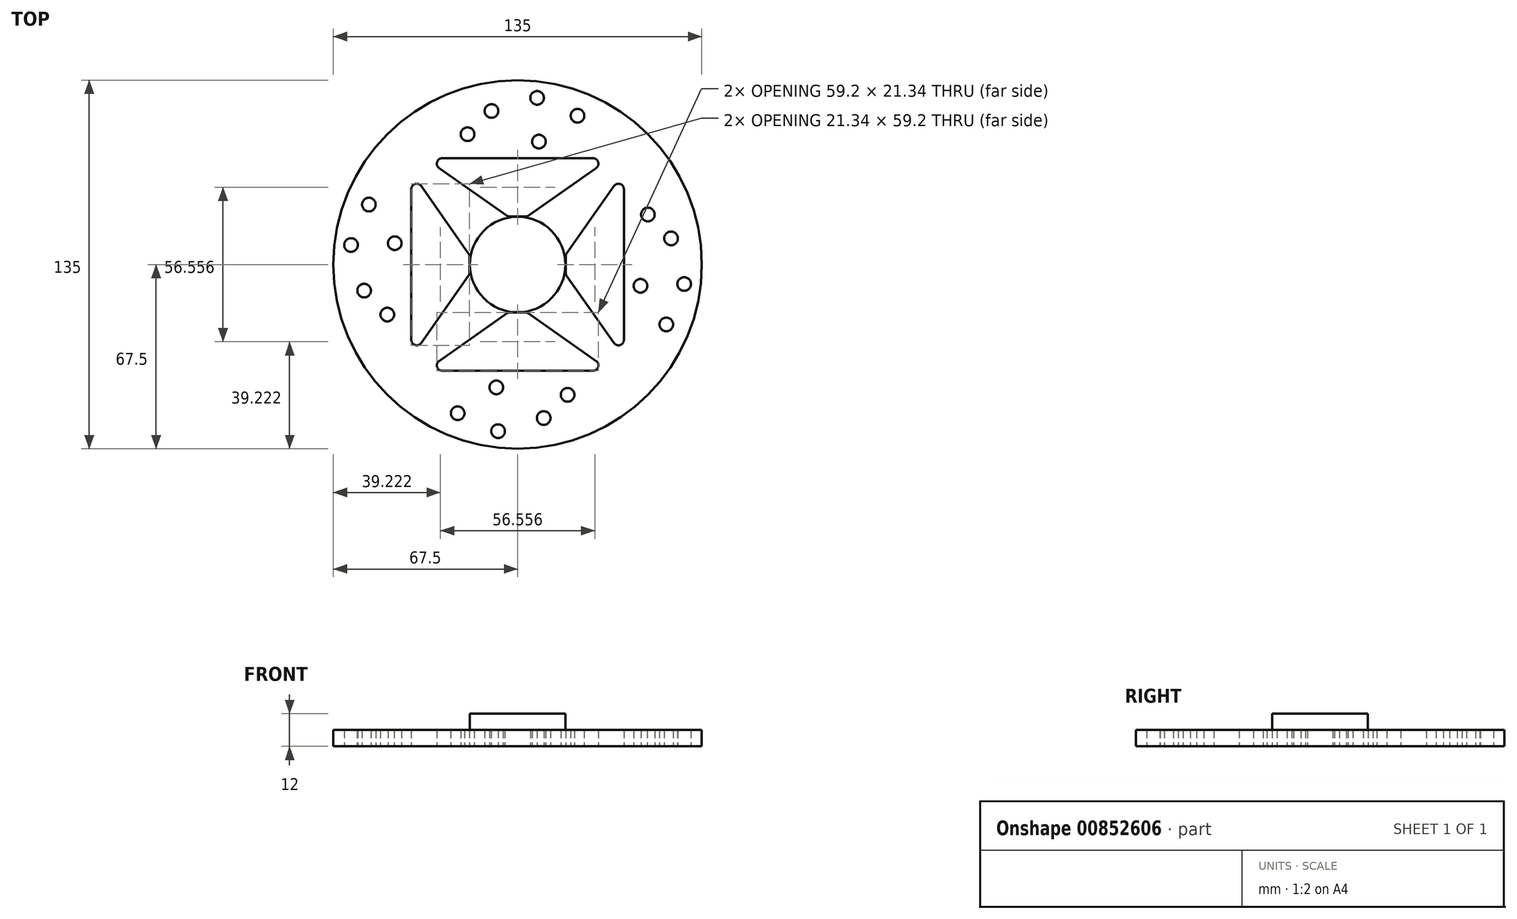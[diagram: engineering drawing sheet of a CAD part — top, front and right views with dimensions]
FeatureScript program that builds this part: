
annotation { "Feature Type Name" : "Feature", "Feature Type Description" : "" }
export const myFeature = defineFeature(function(context is Context, id is Id, definition is map)
    precondition{}
    {
        {
            var Q0;
            Q0=qCreatedBy(makeId("Top.planeOp"),FACE);
            var sketch = newSketch(context, id + "F0", { "sketchPlane" : qUnion([Q0])});
            skCircle(sketch, "E0", {"center": v(0, 0) * mm, "radius": 17.5 * mm});
            skCircle(sketch, "E1", {"center": v(0, 0) * mm, "radius": 67.5 * mm});
            skCircle(sketch, "E2", {"center": v(-18.33, 47.74) * mm, "radius": 2.5 * mm});
            skCircle(sketch, "E3", {"center": v(-9.56, 56.23) * mm, "radius": 2.5 * mm});
            skCircle(sketch, "E4", {"center": v(21.95, 54.5) * mm, "radius": 2.5 * mm});
            skCircle(sketch, "E5", {"center": v(7.15, 61.05) * mm, "radius": 2.5 * mm});
            skCircle(sketch, "E6", {"center": v(7.8, 45.02) * mm, "radius": 2.5 * mm});
            skLineSegment(sketch, "E7", {"start": v(4.08, 17.97) * mm, "end": v(28.75, 35.31) * mm});
            skLineSegment(sketch, "E8", {"start": v(27.6, 38.95) * mm, "end": v(0, 38.95) * mm});
            skLineSegment(sketch, "E9", {"start": v(2.93, 17.6) * mm, "end": v(0, 17.6) * mm});
            skPoint(sketch, "E10.visualSharp", {"position": v(3.56, 17.6) * mm});
            skArc(sketch, "E10.filletArc", {"start": v(2.93, 17.6) * mm, "mid": v(3.53, 17.7) * mm, "end": v(4.08, 17.97) * mm});
            skPoint(sketch, "E11.visualSharp", {"position": v(33.93, 38.95) * mm});
            skArc(sketch, "E11.filletArc", {"start": v(28.75, 35.31) * mm, "mid": v(29.5, 37.55) * mm, "end": v(27.6, 38.95) * mm});
            skLineSegment(sketch, "E12.MirrorCS", {"start": v(-27.6, 38.95) * mm, "end": v(0, 38.95) * mm});
            skArc(sketch, "E13.MirrorCS", {"start": v(-28.75, 35.31) * mm, "mid": v(-29.5, 37.55) * mm, "end": v(-27.6, 38.95) * mm});
            skLineSegment(sketch, "E14.MirrorCS", {"start": v(-4.08, 17.97) * mm, "end": v(-28.75, 35.31) * mm});
            skLineSegment(sketch, "E15.MirrorCS", {"start": v(-2.93, 17.6) * mm, "end": v(0, 17.6) * mm});
            skArc(sketch, "E16.MirrorCS", {"start": v(-2.93, 17.6) * mm, "mid": v(-3.53, 17.7) * mm, "end": v(-4.08, 17.97) * mm});
            skLineSegment(sketch, "E17.1.0", {"start": v(-17.6, 2.93) * mm, "end": v(-17.6, 0) * mm});
            skCircle(sketch, "E17.1.1", {"center": v(-45.02, 7.8) * mm, "radius": 2.5 * mm});
            skCircle(sketch, "E17.1.2", {"center": v(-61.05, 7.15) * mm, "radius": 2.5 * mm});
            skLineSegment(sketch, "E17.1.3", {"start": v(-38.95, 27.6) * mm, "end": v(-38.95, 0) * mm});
            skCircle(sketch, "E17.1.4", {"center": v(-47.74, -18.33) * mm, "radius": 2.5 * mm});
            skArc(sketch, "E17.1.5", {"start": v(-35.31, 28.75) * mm, "mid": v(-37.55, 29.5) * mm, "end": v(-38.95, 27.6) * mm});
            skLineSegment(sketch, "E17.1.6", {"start": v(-38.95, -27.6) * mm, "end": v(-38.95, 0) * mm});
            skLineSegment(sketch, "E17.1.7", {"start": v(-17.6, -2.93) * mm, "end": v(-17.6, 0) * mm});
            skCircle(sketch, "E17.1.8", {"center": v(-54.5, 21.95) * mm, "radius": 2.5 * mm});
            skLineSegment(sketch, "E17.1.9", {"start": v(-17.97, 4.08) * mm, "end": v(-35.31, 28.75) * mm});
            skCircle(sketch, "E17.1.10", {"center": v(-56.23, -9.56) * mm, "radius": 2.5 * mm});
            skLineSegment(sketch, "E17.1.11", {"start": v(-17.97, -4.08) * mm, "end": v(-35.31, -28.75) * mm});
            skArc(sketch, "E17.1.12", {"start": v(-35.31, -28.75) * mm, "mid": v(-37.55, -29.5) * mm, "end": v(-38.95, -27.6) * mm});
            skArc(sketch, "E17.1.13", {"start": v(-17.6, 2.93) * mm, "mid": v(-17.7, 3.53) * mm, "end": v(-17.97, 4.08) * mm});
            skArc(sketch, "E17.1.14", {"start": v(-17.6, -2.93) * mm, "mid": v(-17.7, -3.53) * mm, "end": v(-17.97, -4.08) * mm});
            skLineSegment(sketch, "E17.2.0", {"start": v(-2.93, -17.6) * mm, "end": v(0, -17.6) * mm});
            skCircle(sketch, "E17.2.1", {"center": v(-7.8, -45.02) * mm, "radius": 2.5 * mm});
            skCircle(sketch, "E17.2.2", {"center": v(-7.15, -61.05) * mm, "radius": 2.5 * mm});
            skLineSegment(sketch, "E17.2.3", {"start": v(-27.6, -38.95) * mm, "end": v(0, -38.95) * mm});
            skCircle(sketch, "E17.2.4", {"center": v(18.33, -47.74) * mm, "radius": 2.5 * mm});
            skArc(sketch, "E17.2.5", {"start": v(-28.75, -35.31) * mm, "mid": v(-29.5, -37.55) * mm, "end": v(-27.6, -38.95) * mm});
            skLineSegment(sketch, "E17.2.6", {"start": v(27.6, -38.95) * mm, "end": v(0, -38.95) * mm});
            skLineSegment(sketch, "E17.2.7", {"start": v(2.93, -17.6) * mm, "end": v(0, -17.6) * mm});
            skCircle(sketch, "E17.2.8", {"center": v(-21.95, -54.5) * mm, "radius": 2.5 * mm});
            skLineSegment(sketch, "E17.2.9", {"start": v(-4.08, -17.97) * mm, "end": v(-28.75, -35.31) * mm});
            skCircle(sketch, "E17.2.10", {"center": v(9.56, -56.23) * mm, "radius": 2.5 * mm});
            skLineSegment(sketch, "E17.2.11", {"start": v(4.08, -17.97) * mm, "end": v(28.75, -35.31) * mm});
            skArc(sketch, "E17.2.12", {"start": v(28.75, -35.31) * mm, "mid": v(29.5, -37.55) * mm, "end": v(27.6, -38.95) * mm});
            skArc(sketch, "E17.2.13", {"start": v(-2.93, -17.6) * mm, "mid": v(-3.53, -17.7) * mm, "end": v(-4.08, -17.97) * mm});
            skArc(sketch, "E17.2.14", {"start": v(2.93, -17.6) * mm, "mid": v(3.53, -17.7) * mm, "end": v(4.08, -17.97) * mm});
            skLineSegment(sketch, "E17.3.0", {"start": v(17.6, -2.93) * mm, "end": v(17.6, 0) * mm});
            skCircle(sketch, "E17.3.1", {"center": v(45.02, -7.8) * mm, "radius": 2.5 * mm});
            skCircle(sketch, "E17.3.2", {"center": v(61.05, -7.15) * mm, "radius": 2.5 * mm});
            skLineSegment(sketch, "E17.3.3", {"start": v(38.95, -27.6) * mm, "end": v(38.95, 0) * mm});
            skCircle(sketch, "E17.3.4", {"center": v(47.74, 18.33) * mm, "radius": 2.5 * mm});
            skArc(sketch, "E17.3.5", {"start": v(35.31, -28.75) * mm, "mid": v(37.55, -29.5) * mm, "end": v(38.95, -27.6) * mm});
            skLineSegment(sketch, "E17.3.6", {"start": v(38.95, 27.6) * mm, "end": v(38.95, 0) * mm});
            skLineSegment(sketch, "E17.3.7", {"start": v(17.6, 2.93) * mm, "end": v(17.6, 0) * mm});
            skCircle(sketch, "E17.3.8", {"center": v(54.5, -21.95) * mm, "radius": 2.5 * mm});
            skLineSegment(sketch, "E17.3.9", {"start": v(17.97, -4.08) * mm, "end": v(35.31, -28.75) * mm});
            skCircle(sketch, "E17.3.10", {"center": v(56.23, 9.56) * mm, "radius": 2.5 * mm});
            skLineSegment(sketch, "E17.3.11", {"start": v(17.97, 4.08) * mm, "end": v(35.31, 28.75) * mm});
            skArc(sketch, "E17.3.12", {"start": v(35.31, 28.75) * mm, "mid": v(37.55, 29.5) * mm, "end": v(38.95, 27.6) * mm});
            skArc(sketch, "E17.3.13", {"start": v(17.6, -2.93) * mm, "mid": v(17.7, -3.53) * mm, "end": v(17.97, -4.08) * mm});
            skArc(sketch, "E17.3.14", {"start": v(17.6, 2.93) * mm, "mid": v(17.7, 3.53) * mm, "end": v(17.97, 4.08) * mm});
            skSolve(sketch);
        }
        {
            var Q0;
            Q0=makeQuery(id+"F0.imprint","IMPRINT",FACE,{"disambiguationData":[TD([[makeQuery(id+"F0.imprint","IMPRINT",EDGE,{"derivedFrom":sQuery(id+"F0.wireOp",EDGE,"E0")}),-1.0]])]});
            var sketch = newSketch(context, id + "F1", { "sketchPlane" : qUnion([Q0])});
            skSolve(sketch);
        }
        {
            var Q0;
            Q0=makeQuery(id+"F1.imprint","IMPRINT",FACE,{"disambiguationData":[TD([[makeQuery(id+"F1.imprint","IMPRINT",EDGE,{"derivedFrom":makeQuery(id+"F0.imprint","IMPRINT",EDGE,{"derivedFrom":sQuery(id+"F0.wireOp",EDGE,"E0")})}),-1.0]])]});
            extrude(context, id + "F2", {"entities" : qUnion([Q0]), "depth" : 6 * mm, "offsetDistance" : 25 * mm});
        }
        {
            var Q0;
            Q0=makeQuery(id+"F0.imprint","IMPRINT",FACE,{"disambiguationData":[TD([[makeQuery(id+"F0.imprint","IMPRINT",EDGE,{"derivedFrom":sQuery(id+"F0.wireOp",EDGE,"E0")}),1.0]])]});
            extrude(context, id + "F3", {"entities" : qUnion([Q0]), "operationType" : NewBodyOperationType.ADD, "depth" : 12 * mm, "offsetDistance" : 25 * mm});
        }
    });
